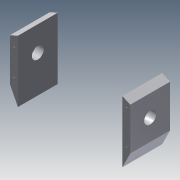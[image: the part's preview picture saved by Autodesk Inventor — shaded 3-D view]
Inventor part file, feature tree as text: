
AUTODESK INVENTOR PART (.ipt)
format: ipt  version: 2013 (Build 170138000, 138)  size: 110,592 bytes
history: native  units: mm
features: sketch x8, hole x4, extrude x1
ambient origin geometry x8: Origin, YZ Plane, XZ Plane, XY Plane, X Axis, Y Axis, Z Axis, Center Point
bodies: Solid1 (feature_tree)
feature tree (13):
  sketch  "Sketch1"  dims[d3=10.0mm d4=53.0mm]
  sketch  "Sketch2"  dims[d8=10.0mm d9=53.0mm]
  sketch  "Sketch3"  dims[d11=50.0mm d12=0.0mm d15=15.0mm]
  extrude  "Extrusion1"  Depth=53.0mm
  hole  "Hole1"  [1 undecoded]
  hole  "Hole2"  [1 undecoded]
  hole  "Hole3"  [1 undecoded]
  sketch  "Sketch7"  dims[d47=2.0mm d48=6.0mm d49=4.0mm d50=2.0mm d51=90.0deg d52=50.0mm d53=0.0mm]
  hole  "Hole4"  [1 undecoded]
  sketch  "Sketch4"  dims[d16=15.0mm d17=6.0mm d18=4.0mm d19=2.0mm d20=90.0deg d21=151.0mm d22=0.0mm]
  sketch  "Sketch5"  dims[d25=2.0mm d26=6.0mm d27=4.0mm d28=2.0mm d29=90.0deg d30=50.0mm d31=0.0mm]
  sketch  "Sketch6"  dims[d34=2.0mm d35=6.0mm d36=4.0mm d37=2.0mm d38=90.0deg d39=50.0mm d40=0.0mm]
  sketch  "Sketch8"
note: 4 required parameter values undecoded (feature->parameter linkage not recoverable at this tier; creation-order binding heuristic only, values carry confidence <= 0.55)
